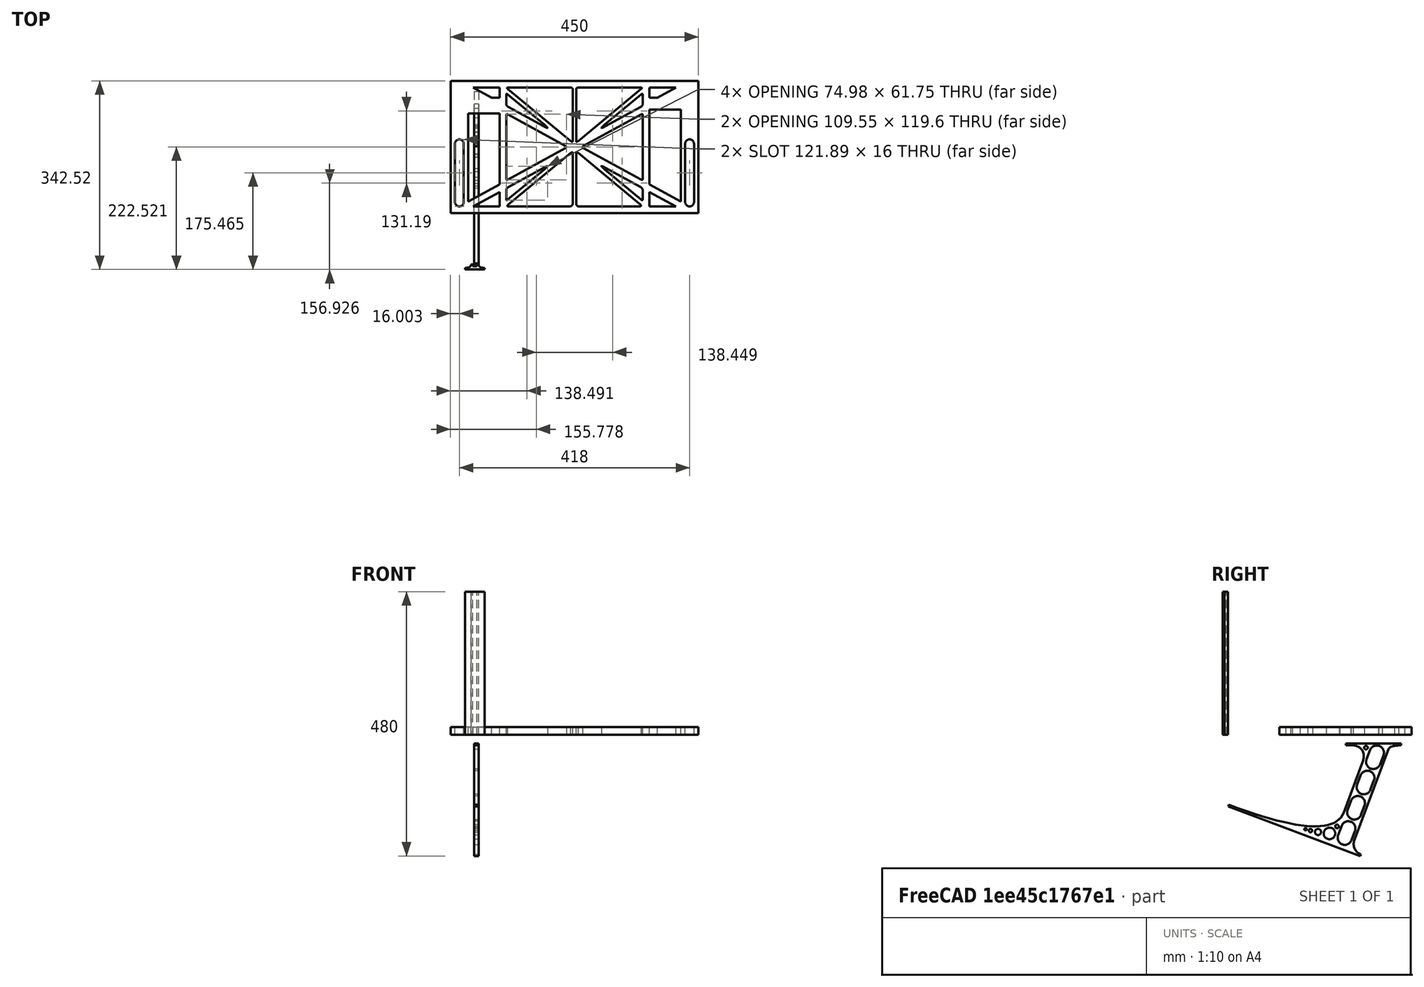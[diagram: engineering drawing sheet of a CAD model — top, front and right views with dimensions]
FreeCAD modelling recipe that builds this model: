
FCSTD DOCUMENT  (FreeCAD 0.19R0.19.2)
Label: laptopStand097
License: All rights reserved
LicenseURL: http://en.wikipedia.org/wiki/All_rights_reserved
objects: Sketcher::SketchObject×3, Part::Extrusion×3
note: 6 computed .brp shape members not serialized (recipe doc carries the construction recipe); baked Part::Feature solids carry a one-line shape summary decoded from their .brp

FEATURE [Sketcher::SketchObject] Sketch
  FullyConstrained = false
  sketch-geometry (252):
    g0: LineSegment StartX=-10.9272 StartY=-82.7794 StartZ=0 EndX=46.0728 EndY=-51.4823 EndZ=0
    g1: LineSegment StartX=366.073 StartY=-91.7794 StartZ=0 EndX=318.073 EndY=-65.424 EndZ=0
    g2: LineSegment StartX=-10.9272 StartY=77.3346 StartZ=0 EndX=-10.9272 EndY=-82.7794 EndZ=0
    g3: LineSegment StartX=375.073 StartY=-82.7794 StartZ=0 EndX=375.073 EndY=83.9235 EndZ=0
    g4: LineSegment StartX=-1.92719 StartY=-91.7794 StartZ=0 EndX=46.0728 EndY=-91.7794 EndZ=0
    g5: LineSegment StartX=318.073 StartY=124.221 StartZ=0 EndX=366.073 EndY=124.221 EndZ=0
    g6: LineSegment StartX=318.073 StartY=83.9235 StartZ=0 EndX=318.073 EndY=-51.4823 EndZ=0
    g7: LineSegment StartX=318.073 StartY=-51.4823 StartZ=0 EndX=375.073 EndY=-82.7794 EndZ=0
    g8: LineSegment StartX=318.073 StartY=-65.424 StartZ=0 EndX=318.073 EndY=-91.7794 EndZ=0
    g9: LineSegment StartX=318.073 StartY=-91.7794 StartZ=0 EndX=366.073 EndY=-91.7794 EndZ=0
    g10: LineSegment StartX=46.0728 StartY=-65.424 StartZ=0 EndX=-1.92719 EndY=-91.7794 EndZ=0
    g11: LineSegment StartX=46.0728 StartY=-65.424 StartZ=0 EndX=46.0728 EndY=-91.7794 EndZ=0
    g12: LineSegment StartX=46.0728 StartY=77.3346 StartZ=0 EndX=46.0728 EndY=-51.4823 EndZ=0
    g13: LineSegment StartX=-42.9272 StartY=136.221 StartZ=0 EndX=-42.9272 EndY=-103.779 EndZ=0
    g14: LineSegment StartX=407.073 StartY=136.221 StartZ=0 EndX=407.073 EndY=-103.779 EndZ=0
    g15: ArcOfCircle CenterX=-26.9272 CenterY=22.1087 CenterZ=0 NormalX=0 NormalY=0 NormalZ=1 AngleXU=0 Radius=8 StartAngle=1e-16 EndAngle=3.14159
    g16: ArcOfCircle CenterX=-26.9272 CenterY=-83.7794 CenterZ=0 NormalX=0 NormalY=0 NormalZ=1 AngleXU=0 Radius=8 StartAngle=3.14159 EndAngle=6.28319
    g17: LineSegment StartX=-34.9272 StartY=22.1087 StartZ=0 EndX=-34.9272 EndY=-83.7794 EndZ=0
    g18: LineSegment StartX=-18.9272 StartY=22.1087 StartZ=0 EndX=-18.9272 EndY=-83.7794 EndZ=0
    g19: ArcOfCircle CenterX=391.073 CenterY=22.1087 CenterZ=0 NormalX=0 NormalY=0 NormalZ=1 AngleXU=0 Radius=8 StartAngle=-4.4e-15 EndAngle=3.14159
    g20: LineSegment StartX=399.073 StartY=22.1087 StartZ=0 EndX=399.073 EndY=-83.7794 EndZ=0
    g21: LineSegment StartX=383.073 StartY=22.1087 StartZ=0 EndX=383.073 EndY=-83.7794 EndZ=0
    g22: ArcOfCircle CenterX=391.073 CenterY=-83.7794 CenterZ=0 NormalX=0 NormalY=0 NormalZ=1 AngleXU=0 Radius=8 StartAngle=3.14159 EndAngle=6.28319
    g23: Circle CenterX=175.022 CenterY=27.0628 CenterZ=0 NormalX=0 NormalY=0 NormalZ=1 AngleXU=0 Radius=1
    g24: Circle CenterX=179.022 CenterY=24.8665 CenterZ=0 NormalX=0 NormalY=0 NormalZ=1 AngleXU=0 Radius=1
    g25: Circle CenterX=179.022 CenterY=27.0628 CenterZ=0 NormalX=0 NormalY=0 NormalZ=1 AngleXU=0 Radius=1
    g26: BSplineCurve PolesCount=3 KnotsCount=2 Degree=2 IsPeriodic=0
    g27: GeomPoint X=175.022 Y=27.0628 Z=0
    g28: GeomPoint X=179.022 Y=27.0628 Z=0
    g29: Circle CenterX=189.124 CenterY=27.0628 CenterZ=0 NormalX=0 NormalY=0 NormalZ=1 AngleXU=0 Radius=1
    g30: Circle CenterX=185.124 CenterY=24.8665 CenterZ=0 NormalX=0 NormalY=0 NormalZ=1 AngleXU=0 Radius=1
    g31: Circle CenterX=185.124 CenterY=27.0628 CenterZ=0 NormalX=0 NormalY=0 NormalZ=1 AngleXU=0 Radius=1
    g32: BSplineCurve PolesCount=3 KnotsCount=2 Degree=2 IsPeriodic=0
    g33: GeomPoint X=189.124 Y=27.0628 Z=0
    g34: GeomPoint X=185.124 Y=27.0628 Z=0
    g35: Circle CenterX=175.022 CenterY=5.37834 CenterZ=0 NormalX=0 NormalY=0 NormalZ=1 AngleXU=0 Radius=1
    g36: Circle CenterX=179.022 CenterY=7.57463 CenterZ=0 NormalX=0 NormalY=0 NormalZ=1 AngleXU=0 Radius=1
    g37: Circle CenterX=179.022 CenterY=5.34704 CenterZ=0 NormalX=0 NormalY=0 NormalZ=1 AngleXU=0 Radius=1
    g38: BSplineCurve PolesCount=3 KnotsCount=2 Degree=2 IsPeriodic=0
    g39: GeomPoint X=175.022 Y=5.37834 Z=0
    g40: GeomPoint X=179.022 Y=5.34704 Z=0
    g41: Circle CenterX=189.124 CenterY=5.37834 CenterZ=0 NormalX=0 NormalY=0 NormalZ=1 AngleXU=0 Radius=1
    g42: Circle CenterX=185.124 CenterY=7.57463 CenterZ=0 NormalX=0 NormalY=0 NormalZ=1 AngleXU=0 Radius=1
    g43: Circle CenterX=185.124 CenterY=5.34704 CenterZ=0 NormalX=0 NormalY=0 NormalZ=1 AngleXU=0 Radius=1
    g44: BSplineCurve PolesCount=3 KnotsCount=2 Degree=2 IsPeriodic=0
    g45: GeomPoint X=189.124 Y=5.37834 Z=0
    g46: GeomPoint X=185.124 Y=5.34704 Z=0
    g47: Circle CenterX=165.871 CenterY=18.1458 CenterZ=0 NormalX=0 NormalY=0 NormalZ=1 AngleXU=0 Radius=1
    g48: Circle CenterX=169.377 CenterY=16.2206 CenterZ=0 NormalX=0 NormalY=0 NormalZ=1 AngleXU=0 Radius=1
    g49: Circle CenterX=165.871 CenterY=14.2954 CenterZ=0 NormalX=0 NormalY=0 NormalZ=1 AngleXU=0 Radius=1
    g50: BSplineCurve PolesCount=3 KnotsCount=2 Degree=2 IsPeriodic=0
    g51: GeomPoint X=165.871 Y=18.1458 Z=0
    g52: GeomPoint X=165.871 Y=14.2954 Z=0
    g53: Circle CenterX=198.275 CenterY=18.1458 CenterZ=0 NormalX=0 NormalY=0 NormalZ=1 AngleXU=0 Radius=1
    g54: Circle CenterX=194.768 CenterY=16.2206 CenterZ=0 NormalX=0 NormalY=0 NormalZ=1 AngleXU=0 Radius=1
    g55: Circle CenterX=198.275 CenterY=14.2954 CenterZ=0 NormalX=0 NormalY=0 NormalZ=1 AngleXU=0 Radius=1
    g56: BSplineCurve PolesCount=3 KnotsCount=2 Degree=2 IsPeriodic=0
    g57: GeomPoint X=198.275 Y=18.1458 Z=0
    g58: GeomPoint X=198.275 Y=14.2954 Z=0
    g59: LineSegment StartX=407.073 StartY=-103.779 StartZ=0 EndX=-42.9272 EndY=-103.779 EndZ=0
    g60: LineSegment StartX=407.073 StartY=136.221 StartZ=0 EndX=-42.9272 EndY=136.221 EndZ=0
    g61: LineSegment StartX=46.0728 StartY=77.3346 StartZ=0 EndX=-10.9272 EndY=77.3346 EndZ=0
    g62: LineSegment StartX=46.0728 StartY=105.865 StartZ=0 EndX=31.5028 EndY=105.865 EndZ=0
    g63: LineSegment StartX=46.0728 StartY=124.221 StartZ=0 EndX=46.0728 EndY=105.865 EndZ=0
    g64: LineSegment StartX=-1.92719 StartY=124.221 StartZ=0 EndX=31.5028 EndY=105.865 EndZ=0
    g65: LineSegment StartX=46.0728 StartY=124.221 StartZ=0 EndX=-1.92719 EndY=124.221 EndZ=0
    g66: LineSegment StartX=318.073 StartY=83.9235 StartZ=0 EndX=375.073 EndY=83.9235 EndZ=0
    g67: Circle CenterX=125.607 CenterY=54.1951 CenterZ=0 NormalX=0 NormalY=0 NormalZ=1 AngleXU=0 Radius=1
    g68: Circle CenterX=139.632 CenterY=46.4944 CenterZ=0 NormalX=0 NormalY=0 NormalZ=1 AngleXU=0 Radius=1
    g69: Circle CenterX=127.326 CenterY=56.7187 CenterZ=0 NormalX=0 NormalY=0 NormalZ=1 AngleXU=0 Radius=1
    g70: BSplineCurve PolesCount=3 KnotsCount=2 Degree=2 IsPeriodic=0
    g71: GeomPoint X=125.607 Y=54.1951 Z=0
    g72: GeomPoint X=127.326 Y=56.7187 Z=0
    g73: Circle CenterX=236.821 CenterY=56.7187 CenterZ=0 NormalX=0 NormalY=0 NormalZ=1 AngleXU=0 Radius=1
    g74: Circle CenterX=224.513 CenterY=46.4944 CenterZ=0 NormalX=0 NormalY=0 NormalZ=1 AngleXU=0 Radius=1
    g75: Circle CenterX=238.538 CenterY=54.1951 CenterZ=0 NormalX=0 NormalY=0 NormalZ=1 AngleXU=0 Radius=1
    g76: BSplineCurve PolesCount=3 KnotsCount=2 Degree=2 IsPeriodic=0
    g77: GeomPoint X=236.821 Y=56.7187 Z=0
    g78: GeomPoint X=238.538 Y=54.1951 Z=0
    g79: Circle CenterX=238.538 CenterY=-21.7539 CenterZ=0 NormalX=0 NormalY=0 NormalZ=1 AngleXU=0 Radius=1
    g80: Circle CenterX=224.513 CenterY=-14.0532 CenterZ=0 NormalX=0 NormalY=0 NormalZ=1 AngleXU=0 Radius=1
    g81: Circle CenterX=236.821 CenterY=-24.2775 CenterZ=0 NormalX=0 NormalY=0 NormalZ=1 AngleXU=0 Radius=1
    g82: BSplineCurve PolesCount=3 KnotsCount=2 Degree=2 IsPeriodic=0
    g83: GeomPoint X=238.538 Y=-21.7539 Z=0
    g84: GeomPoint X=236.821 Y=-24.2775 Z=0
    g85: Circle CenterX=125.607 CenterY=-21.7539 CenterZ=0 NormalX=0 NormalY=0 NormalZ=1 AngleXU=0 Radius=1
    g86: Circle CenterX=139.632 CenterY=-14.0532 CenterZ=0 NormalX=0 NormalY=0 NormalZ=1 AngleXU=0 Radius=1
    g87: Circle CenterX=127.325 CenterY=-24.2775 CenterZ=0 NormalX=0 NormalY=0 NormalZ=1 AngleXU=0 Radius=1
    g88: BSplineCurve PolesCount=3 KnotsCount=2 Degree=2 IsPeriodic=0
    g89: GeomPoint X=125.607 Y=-21.7539 Z=0
    g90: GeomPoint X=127.325 Y=-24.2775 Z=0
    g91: Circle CenterX=302.996 CenterY=111.695 CenterZ=0 NormalX=0 NormalY=0 NormalZ=1 AngleXU=0 Radius=1
    g92: Circle CenterX=306.073 CenterY=114.251 CenterZ=0 NormalX=0 NormalY=0 NormalZ=1 AngleXU=0 Radius=1
    g93: Circle CenterX=306.073 CenterY=110.251 CenterZ=0 NormalX=0 NormalY=0 NormalZ=1 AngleXU=0 Radius=1
    g94: BSplineCurve PolesCount=3 KnotsCount=2 Degree=2 IsPeriodic=0
    g95: GeomPoint X=302.996 Y=111.695 Z=0
    g96: GeomPoint X=306.073 Y=110.251 Z=0
    g97: Circle CenterX=306.073 CenterY=95.2763 CenterZ=0 NormalX=0 NormalY=0 NormalZ=1 AngleXU=0 Radius=1
    g98: Circle CenterX=306.073 CenterY=91.2763 CenterZ=0 NormalX=0 NormalY=0 NormalZ=1 AngleXU=0 Radius=1
    g99: Circle CenterX=302.567 CenterY=89.3511 CenterZ=0 NormalX=0 NormalY=0 NormalZ=1 AngleXU=0 Radius=1
    g100: BSplineCurve PolesCount=3 KnotsCount=2 Degree=2 IsPeriodic=0
    g101: GeomPoint X=306.073 Y=95.2763 Z=0
    g102: GeomPoint X=302.567 Y=89.3511 Z=0
    g103: LineSegment StartX=306.073 StartY=110.251 StartZ=0 EndX=306.073 EndY=95.2763 EndZ=0
    g104: LineSegment StartX=302.996 StartY=111.695 StartZ=0 EndX=236.821 EndY=56.7187 EndZ=0
    g105: LineSegment StartX=238.538 StartY=54.1951 StartZ=0 EndX=302.567 EndY=89.3511 EndZ=0
    g106: Circle CenterX=61.1496 CenterY=111.695 CenterZ=0 NormalX=0 NormalY=0 NormalZ=1 AngleXU=0 Radius=1
    g107: Circle CenterX=58.0728 CenterY=114.251 CenterZ=0 NormalX=0 NormalY=0 NormalZ=1 AngleXU=0 Radius=1
    g108: Circle CenterX=58.0728 CenterY=110.251 CenterZ=0 NormalX=0 NormalY=0 NormalZ=1 AngleXU=0 Radius=1
    g109: BSplineCurve PolesCount=3 KnotsCount=2 Degree=2 IsPeriodic=0
    g110: GeomPoint X=61.1496 Y=111.695 Z=0
    g111: GeomPoint X=58.0728 Y=110.251 Z=0
    g112: Circle CenterX=61.5791 CenterY=89.3511 CenterZ=0 NormalX=0 NormalY=0 NormalZ=1 AngleXU=0 Radius=1
    g113: Circle CenterX=58.0728 CenterY=91.2763 CenterZ=0 NormalX=0 NormalY=0 NormalZ=1 AngleXU=0 Radius=1
    g114: Circle CenterX=58.0728 CenterY=95.2763 CenterZ=0 NormalX=0 NormalY=0 NormalZ=1 AngleXU=0 Radius=1
    g115: BSplineCurve PolesCount=3 KnotsCount=2 Degree=2 IsPeriodic=0
    g116: GeomPoint X=61.5791 Y=89.3511 Z=0
    g117: GeomPoint X=58.0728 Y=95.2763 Z=0
    g118: LineSegment StartX=58.0728 StartY=110.251 StartZ=0 EndX=58.0728 EndY=95.2763 EndZ=0
    g119: LineSegment StartX=61.1496 StartY=111.695 StartZ=0 EndX=127.326 EndY=56.7187 EndZ=0
    g120: LineSegment StartX=125.607 StartY=54.1951 StartZ=0 EndX=61.5791 EndY=89.3511 EndZ=0
    g121: Circle CenterX=61.5791 CenterY=-56.9099 CenterZ=0 NormalX=0 NormalY=0 NormalZ=1 AngleXU=0 Radius=1
    g122: Circle CenterX=58.0728 CenterY=-58.8351 CenterZ=0 NormalX=0 NormalY=0 NormalZ=1 AngleXU=0 Radius=1
    g123: Circle CenterX=58.0728 CenterY=-62.8351 CenterZ=0 NormalX=0 NormalY=0 NormalZ=1 AngleXU=0 Radius=1
    g124: BSplineCurve PolesCount=3 KnotsCount=2 Degree=2 IsPeriodic=0
    g125: GeomPoint X=61.5791 Y=-56.9099 Z=0
    g126: GeomPoint X=58.0728 Y=-62.8351 Z=0
    g127: Circle CenterX=58.0728 CenterY=-77.8102 CenterZ=0 NormalX=0 NormalY=0 NormalZ=1 AngleXU=0 Radius=1
    g128: Circle CenterX=58.0728 CenterY=-81.8102 CenterZ=0 NormalX=0 NormalY=0 NormalZ=1 AngleXU=0 Radius=1
    g129: Circle CenterX=61.1496 CenterY=-79.2541 CenterZ=0 NormalX=0 NormalY=0 NormalZ=1 AngleXU=0 Radius=1
    g130: BSplineCurve PolesCount=3 KnotsCount=2 Degree=2 IsPeriodic=0
    g131: GeomPoint X=58.0728 Y=-77.8102 Z=0
    g132: GeomPoint X=61.1496 Y=-79.2541 Z=0
    g133: LineSegment StartX=58.0728 StartY=-62.8351 StartZ=0 EndX=58.0728 EndY=-77.8102 EndZ=0
    g134: LineSegment StartX=61.1496 StartY=-79.2541 StartZ=0 EndX=127.325 EndY=-24.2775 EndZ=0
    g135: LineSegment StartX=125.607 StartY=-21.7539 StartZ=0 EndX=61.5791 EndY=-56.9099 EndZ=0
    g136: Circle CenterX=302.567 CenterY=-56.9099 CenterZ=0 NormalX=0 NormalY=0 NormalZ=1 AngleXU=0 Radius=1
    g137: Circle CenterX=306.073 CenterY=-58.8351 CenterZ=0 NormalX=0 NormalY=0 NormalZ=1 AngleXU=0 Radius=1
    g138: Circle CenterX=306.073 CenterY=-62.8351 CenterZ=0 NormalX=0 NormalY=0 NormalZ=1 AngleXU=0 Radius=1
    g139: BSplineCurve PolesCount=3 KnotsCount=2 Degree=2 IsPeriodic=0
    g140: GeomPoint X=302.567 Y=-56.9099 Z=0
    g141: GeomPoint X=306.073 Y=-62.8351 Z=0
    g142: Circle CenterX=302.996 CenterY=-79.2541 CenterZ=0 NormalX=0 NormalY=0 NormalZ=1 AngleXU=0 Radius=1
    g143: Circle CenterX=306.073 CenterY=-81.8102 CenterZ=0 NormalX=0 NormalY=0 NormalZ=1 AngleXU=0 Radius=1
    g144: Circle CenterX=306.073 CenterY=-77.8102 CenterZ=0 NormalX=0 NormalY=0 NormalZ=1 AngleXU=0 Radius=1
    g145: BSplineCurve PolesCount=3 KnotsCount=2 Degree=2 IsPeriodic=0
    g146: GeomPoint X=302.996 Y=-79.2541 Z=0
    g147: GeomPoint X=306.073 Y=-77.8102 Z=0
    g148: LineSegment StartX=306.073 StartY=-62.8351 StartZ=0 EndX=306.073 EndY=-77.8102 EndZ=0
    g149: LineSegment StartX=302.996 StartY=-79.2541 StartZ=0 EndX=236.821 EndY=-24.2775 EndZ=0
    g150: LineSegment StartX=238.538 StartY=-21.7539 StartZ=0 EndX=302.567 EndY=-56.9099 EndZ=0
    g151: Circle CenterX=61.6457 CenterY=-88.8112 CenterZ=0 NormalX=0 NormalY=0 NormalZ=1 AngleXU=0 Radius=1
    g152: Circle CenterX=58.0728 CenterY=-91.7794 CenterZ=0 NormalX=0 NormalY=0 NormalZ=1 AngleXU=0 Radius=1
    g153: Circle CenterX=63.9135 CenterY=-91.7794 CenterZ=0 NormalX=0 NormalY=0 NormalZ=1 AngleXU=0 Radius=1
    g154: BSplineCurve PolesCount=3 KnotsCount=2 Degree=2 IsPeriodic=0
    g155: GeomPoint X=61.6457 Y=-88.8112 Z=0
    g156: GeomPoint X=63.9135 Y=-91.7794 Z=0
    g157: Circle CenterX=179.022 CenterY=-85.8163 CenterZ=0 NormalX=0 NormalY=0 NormalZ=1 AngleXU=0 Radius=1
    g158: Circle CenterX=179.022 CenterY=-91.7794 CenterZ=0 NormalX=0 NormalY=0 NormalZ=1 AngleXU=0 Radius=1
    g159: Circle CenterX=171.895 CenterY=-91.7794 CenterZ=0 NormalX=0 NormalY=0 NormalZ=1 AngleXU=0 Radius=1
    g160: BSplineCurve PolesCount=3 KnotsCount=2 Degree=2 IsPeriodic=0
    g161: GeomPoint X=179.022 Y=-85.8163 Z=0
    g162: GeomPoint X=171.895 Y=-91.7794 Z=0
    g163: Circle CenterX=185.124 CenterY=-86.2028 CenterZ=0 NormalX=0 NormalY=0 NormalZ=1 AngleXU=0 Radius=1
    g164: Circle CenterX=185.124 CenterY=-91.7794 CenterZ=0 NormalX=0 NormalY=0 NormalZ=1 AngleXU=0 Radius=1
    g165: Circle CenterX=191.747 CenterY=-91.7794 CenterZ=0 NormalX=0 NormalY=0 NormalZ=1 AngleXU=0 Radius=1
    g166: BSplineCurve PolesCount=3 KnotsCount=2 Degree=2 IsPeriodic=0
    g167: GeomPoint X=185.124 Y=-86.2028 Z=0
    g168: GeomPoint X=191.747 Y=-91.7794 Z=0
    g169: Circle CenterX=299.888 CenterY=-86.6413 CenterZ=0 NormalX=0 NormalY=0 NormalZ=1 AngleXU=0 Radius=1
    g170: Circle CenterX=306.073 CenterY=-91.7794 CenterZ=0 NormalX=0 NormalY=0 NormalZ=1 AngleXU=0 Radius=1
    g171: Circle CenterX=298.776 CenterY=-91.7794 CenterZ=0 NormalX=0 NormalY=0 NormalZ=1 AngleXU=0 Radius=1
    g172: BSplineCurve PolesCount=3 KnotsCount=2 Degree=2 IsPeriodic=0
    g173: GeomPoint X=299.888 Y=-86.6413 Z=0
    g174: GeomPoint X=298.776 Y=-91.7794 Z=0
    g175: LineSegment StartX=189.124 StartY=5.37834 StartZ=0 EndX=299.888 EndY=-86.6413 EndZ=0
    g176: LineSegment StartX=298.776 StartY=-91.7794 StartZ=0 EndX=191.747 EndY=-91.7794 EndZ=0
    g177: LineSegment StartX=185.124 StartY=-86.2028 StartZ=0 EndX=185.124 EndY=5.34704 EndZ=0
    g178: LineSegment StartX=179.022 StartY=5.34704 StartZ=0 EndX=179.022 EndY=-85.8163 EndZ=0
    g179: LineSegment StartX=171.895 StartY=-91.7794 StartZ=0 EndX=63.9135 EndY=-91.7794 EndZ=0
    g180: LineSegment StartX=61.6457 StartY=-88.8112 StartZ=0 EndX=175.022 EndY=5.37834 EndZ=0
    g181: Circle CenterX=302.073 CenterY=124.221 CenterZ=0 NormalX=0 NormalY=0 NormalZ=1 AngleXU=0 Radius=1
    g182: Circle CenterX=306.073 CenterY=124.221 CenterZ=0 NormalX=0 NormalY=0 NormalZ=1 AngleXU=0 Radius=1
    g183: Circle CenterX=302.996 CenterY=121.665 CenterZ=0 NormalX=0 NormalY=0 NormalZ=1 AngleXU=0 Radius=1
    g184: BSplineCurve PolesCount=3 KnotsCount=2 Degree=2 IsPeriodic=0
    g185: GeomPoint X=302.073 Y=124.221 Z=0
    g186: GeomPoint X=302.996 Y=121.665 Z=0
    g187: Circle CenterX=189.124 CenterY=124.221 CenterZ=0 NormalX=0 NormalY=0 NormalZ=1 AngleXU=0 Radius=1
    g188: Circle CenterX=185.124 CenterY=124.221 CenterZ=0 NormalX=0 NormalY=0 NormalZ=1 AngleXU=0 Radius=1
    g189: Circle CenterX=185.124 CenterY=120.221 CenterZ=0 NormalX=0 NormalY=0 NormalZ=1 AngleXU=0 Radius=1
    g190: BSplineCurve PolesCount=3 KnotsCount=2 Degree=2 IsPeriodic=0
    g191: GeomPoint X=189.124 Y=124.221 Z=0
    g192: GeomPoint X=185.124 Y=120.221 Z=0
    g193: Circle CenterX=175.022 CenterY=124.221 CenterZ=0 NormalX=0 NormalY=0 NormalZ=1 AngleXU=0 Radius=1
    g194: Circle CenterX=179.022 CenterY=124.221 CenterZ=0 NormalX=0 NormalY=0 NormalZ=1 AngleXU=0 Radius=1
    g195: Circle CenterX=179.022 CenterY=120.221 CenterZ=0 NormalX=0 NormalY=0 NormalZ=1 AngleXU=0 Radius=1
    g196: BSplineCurve PolesCount=3 KnotsCount=2 Degree=2 IsPeriodic=0
    g197: GeomPoint X=175.022 Y=124.221 Z=0
    g198: GeomPoint X=179.022 Y=120.221 Z=0
    g199: Circle CenterX=62.0728 CenterY=124.221 CenterZ=0 NormalX=0 NormalY=0 NormalZ=1 AngleXU=0 Radius=1
    g200: Circle CenterX=58.0728 CenterY=124.221 CenterZ=0 NormalX=0 NormalY=0 NormalZ=1 AngleXU=0 Radius=1
    g201: Circle CenterX=61.1496 CenterY=121.665 CenterZ=0 NormalX=0 NormalY=0 NormalZ=1 AngleXU=0 Radius=1
    g202: BSplineCurve PolesCount=3 KnotsCount=2 Degree=2 IsPeriodic=0
    g203: GeomPoint X=62.0728 Y=124.221 Z=0
    g204: GeomPoint X=61.1496 Y=121.665 Z=0
    g205: LineSegment StartX=62.0728 StartY=124.221 StartZ=0 EndX=175.022 EndY=124.221 EndZ=0
    g206: LineSegment StartX=179.022 StartY=120.221 StartZ=0 EndX=179.022 EndY=27.0628 EndZ=0
    g207: LineSegment StartX=185.124 StartY=27.0628 StartZ=0 EndX=185.124 EndY=120.221 EndZ=0
    g208: LineSegment StartX=189.124 StartY=124.221 StartZ=0 EndX=302.073 EndY=124.221 EndZ=0
    g209: LineSegment StartX=302.996 StartY=121.665 StartZ=0 EndX=189.124 EndY=27.0628 EndZ=0
    g210: LineSegment StartX=175.022 StartY=27.0628 StartZ=0 EndX=61.1496 EndY=121.665 EndZ=0
    g211: Circle CenterX=61.5791 CenterY=75.4095 CenterZ=0 NormalX=0 NormalY=0 NormalZ=1 AngleXU=0 Radius=1
    g212: Circle CenterX=58.0728 CenterY=77.3346 CenterZ=0 NormalX=0 NormalY=0 NormalZ=1 AngleXU=0 Radius=1
    g213: Circle CenterX=58.0728 CenterY=73.3346 CenterZ=0 NormalX=0 NormalY=0 NormalZ=1 AngleXU=0 Radius=1
    g214: BSplineCurve PolesCount=3 KnotsCount=2 Degree=2 IsPeriodic=0
    g215: GeomPoint X=61.5791 Y=75.4095 Z=0
    g216: GeomPoint X=58.0728 Y=73.3346 Z=0
    g217: Circle CenterX=58.0728 CenterY=-40.8935 CenterZ=0 NormalX=0 NormalY=0 NormalZ=1 AngleXU=0 Radius=1
    g218: Circle CenterX=58.0728 CenterY=-44.8935 CenterZ=0 NormalX=0 NormalY=0 NormalZ=1 AngleXU=0 Radius=1
    g219: Circle CenterX=61.5791 CenterY=-42.9683 CenterZ=0 NormalX=0 NormalY=0 NormalZ=1 AngleXU=0 Radius=1
    g220: BSplineCurve PolesCount=3 KnotsCount=2 Degree=2 IsPeriodic=0
    g221: GeomPoint X=58.0728 Y=-40.8935 Z=0
    g222: GeomPoint X=61.5791 Y=-42.9683 Z=0
    g223: LineSegment StartX=61.5791 StartY=-42.9683 StartZ=0 EndX=165.871 EndY=14.2954 EndZ=0
    g224: LineSegment StartX=165.871 StartY=18.1458 StartZ=0 EndX=61.5791 EndY=75.4095 EndZ=0
    g225: LineSegment StartX=58.0728 StartY=73.3346 StartZ=0 EndX=58.0728 EndY=-40.8935 EndZ=0
    g226: Circle CenterX=302.567 CenterY=-42.9683 CenterZ=0 NormalX=0 NormalY=0 NormalZ=1 AngleXU=0 Radius=1
    g227: Circle CenterX=306.073 CenterY=-44.8935 CenterZ=0 NormalX=0 NormalY=0 NormalZ=1 AngleXU=0 Radius=1
    g228: Circle CenterX=306.073 CenterY=-40.8935 CenterZ=0 NormalX=0 NormalY=0 NormalZ=1 AngleXU=0 Radius=1
    g229: BSplineCurve PolesCount=3 KnotsCount=2 Degree=2 IsPeriodic=0
    g230: GeomPoint X=302.567 Y=-42.9683 Z=0
    g231: GeomPoint X=306.073 Y=-40.8935 Z=0
    g232: Circle CenterX=306.073 CenterY=73.3346 CenterZ=0 NormalX=0 NormalY=0 NormalZ=1 AngleXU=0 Radius=1
    g233: Circle CenterX=306.073 CenterY=77.3346 CenterZ=0 NormalX=0 NormalY=0 NormalZ=1 AngleXU=0 Radius=1
    g234: Circle CenterX=302.567 CenterY=75.4095 CenterZ=0 NormalX=0 NormalY=0 NormalZ=1 AngleXU=0 Radius=1
    g235: BSplineCurve PolesCount=3 KnotsCount=2 Degree=2 IsPeriodic=0
    g236: GeomPoint X=306.073 Y=73.3346 Z=0
    g237: GeomPoint X=302.567 Y=75.4095 Z=0
    g238: LineSegment StartX=302.567 StartY=-42.9683 StartZ=0 EndX=198.275 EndY=14.2954 EndZ=0
    g239: LineSegment StartX=198.275 StartY=18.1458 StartZ=0 EndX=302.567 EndY=75.4095 EndZ=0
    g240: LineSegment StartX=306.073 StartY=73.3346 StartZ=0 EndX=306.073 EndY=-40.8935 EndZ=0
    g241: LineSegment StartX=318.073 StartY=124.221 StartZ=0 EndX=322.073 EndY=124.221 EndZ=0
    g242: LineSegment StartX=366.073 StartY=124.221 StartZ=0 EndX=362.073 EndY=124.221 EndZ=0
    g243: LineSegment StartX=328.643 StartY=105.865 StartZ=0 EndX=332.643 EndY=105.865 EndZ=0
    g244: LineSegment StartX=332.651 StartY=105.853 StartZ=0 EndX=336.157 EndY=107.779 EndZ=0
    g245: LineSegment StartX=366.073 StartY=124.221 StartZ=0 EndX=362.567 EndY=122.294 EndZ=0
    g246: LineSegment StartX=318.073 StartY=105.865 StartZ=0 EndX=318.073 EndY=109.865 EndZ=0
    g247: LineSegment StartX=318.073 StartY=105.865 StartZ=0 EndX=322.073 EndY=105.865 EndZ=0
    g248: LineSegment StartX=318.073 StartY=124.221 StartZ=0 EndX=318.073 EndY=120.221 EndZ=0
    g249: LineSegment StartX=332.651 StartY=105.853 StartZ=0 EndX=366.073 EndY=124.221 EndZ=0
    g250: LineSegment StartX=322.073 StartY=105.865 StartZ=0 EndX=328.643 EndY=105.865 EndZ=0
    g251: LineSegment StartX=318.073 StartY=120.221 StartZ=0 EndX=318.073 EndY=109.865 EndZ=0
  constraints (436):
    c: Horizontal(g4)
    c: Coincident(g6,g7)
    c: Coincident(g8,g1)
    c: Tangent(g6,g8)
    c: Coincident(g11,g10)
    c: Coincident(g0,g12)
    c: Block(g7)
    c: Block(g3)
    c: Block(g1)
    c: Block(g8)
    c: Block(g11)
    c: Block(g10)
    c: Block(g0)
    c: Block(g2)
    c: Block(g5)
    c: Block(g9)
    c: Block(g4)
    c: Vertical(g13)
    c: Vertical(g14)
    c: Block(g14)
    c: Block(g13)
    c: Tangent(g15,g18) = 1.5708
    c: Tangent(g15,g17) = -1.5708
    c: Tangent(g17,g16) = -1.5708
    c: Tangent(g18,g16) = 1.5708
    c: Vertical(g17)
    c: Equal(g15,g16)
    c: Block(g18)
    c: Block(g17)
    c: Tangent(g19,g20) = 1.5708
    c: Tangent(g20,g22) = 1.5708
    c: Equal(g19,g22)
    c: Coincident(g21,g19)
    c: Coincident(g21,g22)
    c: Block(g20)
    c: Block(g21)
    c: Weight(g23) = 1
    c: Equal(g23,g24)
    c: Equal(g23,g25)
    c: InternalAlignment(g23,g26)
    c: InternalAlignment(g24,g26)
    c: InternalAlignment(g25,g26)
    c: InternalAlignment(g27,g26)
    c: InternalAlignment(g28,g26)
    c: Weight(g29) = 1
    c: Equal(g29,g30)
    c: Equal(g29,g31)
    c: InternalAlignment(g29,g32)
    c: InternalAlignment(g30,g32)
    c: InternalAlignment(g31,g32)
    c: InternalAlignment(g33,g32)
    c: InternalAlignment(g34,g32)
    c: Block(g32)
    c: Block(g26)
    c: Weight(g35) = 1
    c: Equal(g35,g36)
    c: Equal(g35,g37)
    c: InternalAlignment(g35,g38)
    c: InternalAlignment(g36,g38)
    c: InternalAlignment(g37,g38)
    c: InternalAlignment(g39,g38)
    c: InternalAlignment(g40,g38)
    c: Weight(g41) = 1
    c: Equal(g41,g42)
    c: Equal(g41,g43)
    c: InternalAlignment(g41,g44)
    c: InternalAlignment(g42,g44)
    c: InternalAlignment(g43,g44)
    c: InternalAlignment(g45,g44)
    c: InternalAlignment(g46,g44)
    c: Block(g44)
    c: Block(g38)
    c: Weight(g47) = 1
    c: Equal(g47,g48)
    c: Equal(g47,g49)
    c: InternalAlignment(g47,g50)
    c: InternalAlignment(g48,g50)
    c: InternalAlignment(g49,g50)
    c: InternalAlignment(g51,g50)
    c: InternalAlignment(g52,g50)
    c: Weight(g53) = 1
    c: Equal(g53,g54)
    c: Equal(g53,g55)
    c: InternalAlignment(g53,g56)
    c: InternalAlignment(g54,g56)
    c: InternalAlignment(g55,g56)
    c: InternalAlignment(g57,g56)
    c: InternalAlignment(g58,g56)
    c: Block(g50)
    c: Block(g56)
    c: Coincident(g59,g14)
    c: Coincident(g59,g13)
    c: Horizontal(g59)
    c: Distance(g59) = 450
    c: Coincident(g60,g14)
    c: Coincident(g60,g13)
    c: Horizontal(g60)
    c: Horizontal(g61)
    c: Coincident(g12,g61)
    c: Horizontal(g62)
    c: Vertical(g63)
    c: Block(g63)
    c: Block(g62)
    c: Block(g61)
    c: Distance(g63) = 18.3554
    c: Coincident(g65,g63)
    c: Coincident(g65,g64)
    c: Horizontal(g65)
    c: Block(g65)
    c: Block(g64)
    c: Coincident(g62,g64)
    c: Coincident(g2,g61)
    c: Coincident(g66,g6)
    c: Horizontal(g66)
    c: Block(g66)
    c: Coincident(g3,g66)
    c: Weight(g67) = 1
    c: Equal(g67,g68)
    c: Equal(g67,g69)
    c: InternalAlignment(g67,g70)
    c: InternalAlignment(g68,g70)
    c: InternalAlignment(g69,g70)
    c: InternalAlignment(g71,g70)
    c: InternalAlignment(g72,g70)
    c: Block(g70)
    c: Weight(g73) = 1
    c: Equal(g73,g74)
    c: Equal(g73,g75)
    c: InternalAlignment(g73,g76)
    c: InternalAlignment(g74,g76)
    c: InternalAlignment(g75,g76)
    c: InternalAlignment(g77,g76)
    c: InternalAlignment(g78,g76)
    c: Block(g76)
    c: Weight(g79) = 1
    c: Equal(g79,g80)
    c: Equal(g79,g81)
    c: InternalAlignment(g79,g82)
    c: InternalAlignment(g80,g82)
    c: InternalAlignment(g81,g82)
    c: InternalAlignment(g83,g82)
    c: InternalAlignment(g84,g82)
    c: Block(g82)
    c: Weight(g85) = 1
    c: Equal(g85,g86)
    c: Equal(g85,g87)
    c: InternalAlignment(g85,g88)
    c: InternalAlignment(g86,g88)
    c: InternalAlignment(g87,g88)
    c: InternalAlignment(g89,g88)
    c: InternalAlignment(g90,g88)
    c: Block(g88)
    c: Weight(g91) = 1
    c: Equal(g91,g92)
    c: Equal(g91,g93)
    c: InternalAlignment(g91,g94)
    c: InternalAlignment(g92,g94)
    c: InternalAlignment(g93,g94)
    c: InternalAlignment(g95,g94)
    c: InternalAlignment(g96,g94)
    c: Weight(g97) = 1
    c: Equal(g97,g98)
    c: Equal(g97,g99)
    c: InternalAlignment(g97,g100)
    c: InternalAlignment(g98,g100)
    c: InternalAlignment(g99,g100)
    c: InternalAlignment(g101,g100)
    c: InternalAlignment(g102,g100)
    c: Block(g94)
    c: Block(g100)
    c: Coincident(g103,g94)
    c: Coincident(g103,g100)
    c: Vertical(g103)
    c: Coincident(g104,g94)
    c: Coincident(g104,g76)
    c: Coincident(g105,g76)
    c: Coincident(g105,g100)
    c: Weight(g106) = 1
    c: Equal(g106,g107)
    c: Equal(g106,g108)
    c: InternalAlignment(g106,g109)
    c: InternalAlignment(g107,g109)
    c: InternalAlignment(g108,g109)
    c: InternalAlignment(g110,g109)
    c: InternalAlignment(g111,g109)
    c: Weight(g112) = 1
    c: Equal(g112,g113)
    c: Equal(g112,g114)
    c: InternalAlignment(g112,g115)
    c: InternalAlignment(g113,g115)
    c: InternalAlignment(g114,g115)
    c: InternalAlignment(g116,g115)
    c: InternalAlignment(g117,g115)
    c: Block(g109)
    c: Block(g115)
    c: Coincident(g118,g109)
    c: Coincident(g118,g115)
    c: Vertical(g118)
    c: Coincident(g119,g109)
    c: Coincident(g119,g70)
    c: Coincident(g120,g70)
    c: Coincident(g120,g115)
    c: Weight(g121) = 1
    c: Equal(g121,g122)
    c: Equal(g121,g123)
    c: InternalAlignment(g121,g124)
    c: InternalAlignment(g122,g124)
    c: InternalAlignment(g123,g124)
    c: InternalAlignment(g125,g124)
    c: InternalAlignment(g126,g124)
    c: Weight(g127) = 1
    c: Equal(g127,g128)
    c: Equal(g127,g129)
    c: InternalAlignment(g127,g130)
    c: InternalAlignment(g128,g130)
    c: InternalAlignment(g129,g130)
    c: InternalAlignment(g131,g130)
    c: InternalAlignment(g132,g130)
    c: Block(g124)
    c: Block(g130)
    c: Coincident(g133,g124)
    c: Coincident(g133,g130)
    c: Vertical(g133)
    c: Coincident(g134,g130)
    c: Coincident(g134,g88)
    c: Coincident(g135,g88)
    c: Coincident(g135,g124)
    c: Weight(g136) = 1
    c: Equal(g136,g137)
    c: Equal(g136,g138)
    c: InternalAlignment(g136,g139)
    c: InternalAlignment(g137,g139)
    c: InternalAlignment(g138,g139)
    c: InternalAlignment(g140,g139)
    c: InternalAlignment(g141,g139)
    c: Weight(g142) = 1
    c: Equal(g142,g143)
    c: Equal(g142,g144)
    c: InternalAlignment(g142,g145)
    c: InternalAlignment(g143,g145)
    c: InternalAlignment(g144,g145)
    c: InternalAlignment(g146,g145)
    c: InternalAlignment(g147,g145)
    c: Block(g139)
    c: Block(g145)
    c: Coincident(g148,g139)
    c: Coincident(g148,g145)
    c: Vertical(g148)
    c: Coincident(g149,g145)
    c: Coincident(g149,g82)
    c: Coincident(g150,g82)
    c: Coincident(g150,g139)
    c: Weight(g151) = 1
    c: Equal(g151,g152)
    c: Equal(g151,g153)
    c: InternalAlignment(g151,g154)
    c: InternalAlignment(g152,g154)
    c: InternalAlignment(g153,g154)
    c: InternalAlignment(g155,g154)
    c: InternalAlignment(g156,g154)
    c: Weight(g157) = 1
    c: Equal(g157,g158)
    c: Equal(g157,g159)
    c: InternalAlignment(g157,g160)
    c: InternalAlignment(g158,g160)
    c: InternalAlignment(g159,g160)
    c: InternalAlignment(g161,g160)
    c: InternalAlignment(g162,g160)
    c: Weight(g163) = 1
    c: Equal(g163,g164)
    c: Equal(g163,g165)
    c: InternalAlignment(g163,g166)
    c: InternalAlignment(g164,g166)
    c: InternalAlignment(g165,g166)
    c: InternalAlignment(g167,g166)
    c: InternalAlignment(g168,g166)
    c: Weight(g169) = 1
    c: Equal(g169,g170)
    c: Equal(g169,g171)
    c: InternalAlignment(g169,g172)
    c: InternalAlignment(g170,g172)
    c: InternalAlignment(g171,g172)
    c: InternalAlignment(g173,g172)
    c: InternalAlignment(g174,g172)
    c: Block(g172)
    c: Block(g166)
    c: Block(g160)
    c: Block(g154)
    c: Coincident(g175,g44)
    c: Coincident(g175,g172)
    c: Coincident(g176,g172)
    c: Coincident(g176,g166)
    c: Horizontal(g176)
    c: Coincident(g177,g166)
    c: Coincident(g177,g44)
    c: Vertical(g177)
    c: Coincident(g178,g38)
    c: Coincident(g178,g160)
    c: Vertical(g178)
    c: Coincident(g179,g160)
    c: Coincident(g179,g154)
    c: Horizontal(g179)
    c: Coincident(g180,g154)
    c: Coincident(g180,g38)
    c: Weight(g181) = 1
    c: Equal(g181,g182)
    c: Equal(g181,g183)
    c: InternalAlignment(g181,g184)
    c: InternalAlignment(g182,g184)
    c: InternalAlignment(g183,g184)
    c: InternalAlignment(g185,g184)
    c: InternalAlignment(g186,g184)
    c: Weight(g187) = 1
    c: Equal(g187,g188)
    c: Equal(g187,g189)
    c: InternalAlignment(g187,g190)
    c: InternalAlignment(g188,g190)
    c: InternalAlignment(g189,g190)
    c: InternalAlignment(g191,g190)
    c: InternalAlignment(g192,g190)
    c: Weight(g193) = 1
    c: Equal(g193,g194)
    c: Equal(g193,g195)
    c: InternalAlignment(g193,g196)
    c: InternalAlignment(g194,g196)
    c: InternalAlignment(g195,g196)
    c: InternalAlignment(g197,g196)
    c: InternalAlignment(g198,g196)
    c: Weight(g199) = 1
    c: Equal(g199,g200)
    c: Equal(g199,g201)
    c: InternalAlignment(g199,g202)
    c: InternalAlignment(g200,g202)
    c: InternalAlignment(g201,g202)
    c: InternalAlignment(g203,g202)
    c: InternalAlignment(g204,g202)
    c: Block(g202)
    c: Block(g196)
    c: Block(g190)
    c: Block(g184)
    c: Coincident(g205,g202)
    c: Coincident(g205,g196)
    c: Horizontal(g205)
    c: Coincident(g206,g196)
    c: Coincident(g206,g26)
    c: Vertical(g206)
    c: Coincident(g207,g32)
    c: Coincident(g207,g190)
    c: Vertical(g207)
    c: Coincident(g208,g190)
    c: Coincident(g208,g184)
    c: Horizontal(g208)
    c: Coincident(g209,g184)
    c: Coincident(g209,g32)
    c: Coincident(g210,g26)
    c: Weight(g211) = 1
    c: Equal(g211,g212)
    c: Equal(g211,g213)
    c: InternalAlignment(g211,g214)
    c: InternalAlignment(g212,g214)
    c: InternalAlignment(g213,g214)
    c: InternalAlignment(g215,g214)
    c: InternalAlignment(g216,g214)
    c: Weight(g217) = 1
    c: Equal(g217,g218)
    c: Equal(g217,g219)
    c: InternalAlignment(g217,g220)
    c: InternalAlignment(g218,g220)
    c: InternalAlignment(g219,g220)
    c: InternalAlignment(g221,g220)
    c: InternalAlignment(g222,g220)
    c: Block(g220)
    c: Block(g214)
    c: Coincident(g223,g220)
    c: Coincident(g223,g50)
    c: Coincident(g224,g50)
    c: Coincident(g224,g214)
    c: Coincident(g225,g214)
    c: Coincident(g225,g220)
    c: Vertical(g225)
    c: Weight(g226) = 1
    c: Equal(g226,g227)
    c: Equal(g226,g228)
    c: InternalAlignment(g226,g229)
    c: InternalAlignment(g227,g229)
    c: InternalAlignment(g228,g229)
    c: InternalAlignment(g230,g229)
    c: InternalAlignment(g231,g229)
    c: Weight(g232) = 1
    c: Equal(g232,g233)
    c: Equal(g232,g234)
    c: InternalAlignment(g232,g235)
    c: InternalAlignment(g233,g235)
    c: InternalAlignment(g234,g235)
    c: InternalAlignment(g236,g235)
    c: InternalAlignment(g237,g235)
    c: Block(g235)
    c: Block(g229)
    c: Coincident(g238,g229)
    c: Coincident(g238,g56)
    c: Coincident(g239,g56)
    c: Coincident(g239,g235)
    c: Coincident(g240,g235)
    c: Coincident(g240,g229)
    c: Vertical(g240)
    c: Horizontal(g241)
    c: Horizontal(g242)
    c: Horizontal(g243)
    c: Vertical(g246)
    c: Horizontal(g247)
    c: Vertical(g248)
    c: Distance(g243) = 4
    c: Distance(g247) = 4
    c: Distance(g246) = 4
    c: Distance(g248) = 4
    c: Distance(g241) = 4
    c: Distance(g242) = 4
    c: Coincident(g241,g5)
    c: Coincident(g248,g5)
    c: Coincident(g5,g242)
    c: Coincident(g249,g5)
    c: Coincident(g250,g247)
    c: Coincident(g250,g243)
    c: Horizontal(g250)
    c: Block(g250)
    c: Coincident(g251,g248)
    c: Coincident(g251,g246)
    c: Vertical(g251)
    c: Block(g251)
    c: Distance(g244) = 4
    c: Distance(g245) = 4
    c: Parallel(g244,g249)
    c: Parallel(g245,g249)
    c: Block(g249)
    c: Coincident(g244,g249)
    c: Coincident(g245,g5)
FEATURE [Sketcher::SketchObject] Sketch001
  FullyConstrained = true
  MapMode = 4
  Placement = pos=(0,0,0) rot=(0.57735,0.57735,0.57735;2.0944rad)
  Support = -> [Sketch]
  sketch-geometry (46):
    g0: BSplineCurve PolesCount=3 KnotsCount=2 Degree=2 IsPeriodic=0
    g1: ArcOfCircle CenterX=73.1223 CenterY=-32.291 CenterZ=0 NormalX=0 NormalY=0 NormalZ=1 AngleXU=0 Radius=13 StartAngle=5.92268 EndAngle=9.06428
    g2: ArcOfCircle CenterX=66.7816 CenterY=-49.1439 CenterZ=0 NormalX=0 NormalY=0 NormalZ=1 AngleXU=0 Radius=13 StartAngle=2.78068 EndAngle=5.92131
    g3: ArcOfCircle CenterX=55.9263 CenterY=-78.1807 CenterZ=0 NormalX=0 NormalY=0 NormalZ=1 AngleXU=0 Radius=13 StartAngle=5.92268 EndAngle=9.06428
    g4: ArcOfCircle CenterX=49.5884 CenterY=-95.0342 CenterZ=0 NormalX=0 NormalY=0 NormalZ=1 AngleXU=0 Radius=13 StartAngle=2.78068 EndAngle=5.92131
    g5: ArcOfCircle CenterX=38.7206 CenterY=-124.067 CenterZ=0 NormalX=0 NormalY=0 NormalZ=1 AngleXU=0 Radius=13 StartAngle=5.92268 EndAngle=9.06428
    g6: ArcOfCircle CenterX=32.3875 CenterY=-140.92 CenterZ=0 NormalX=0 NormalY=0 NormalZ=1 AngleXU=0 Radius=13 StartAngle=2.78068 EndAngle=5.92131
    g7: ArcOfCircle CenterX=21.4715 CenterY=-169.934 CenterZ=0 NormalX=0 NormalY=0 NormalZ=1 AngleXU=0 Radius=13 StartAngle=5.92268 EndAngle=9.06428
    g8: ArcOfCircle CenterX=15.1336 CenterY=-186.787 CenterZ=0 NormalX=0 NormalY=0 NormalZ=1 AngleXU=0 Radius=13 StartAngle=2.78068 EndAngle=5.92131
    g9-g12: Circle x4 (B-spline internal-alignment scaffolding for g13; pole/knot coordinates omitted)
    g13: BSplineCurve PolesCount=4 KnotsCount=2 Degree=3 IsPeriodic=0
    g14: GeomPoint X=28.8094 Y=-19.0875 Z=0
    g15: GeomPoint X=47.0443 Y=-50.4712 Z=0
    g16: Circle CenterX=53.5586 CenterY=-23.2695 CenterZ=0 NormalX=0 NormalY=0 NormalZ=1 AngleXU=0 Radius=3.24518
    g17: Circle CenterX=-195.441 CenterY=-127.082 CenterZ=0 NormalX=0 NormalY=0 NormalZ=1 AngleXU=0 Radius=1
    g18: Circle CenterX=-8.24091 CenterY=-197.481 CenterZ=0 NormalX=0 NormalY=0 NormalZ=1 AngleXU=0 Radius=1
    g19: Circle CenterX=12.8789 CenterY=-141.321 CenterZ=0 NormalX=0 NormalY=0 NormalZ=1 AngleXU=0 Radius=1
    g20: BSplineCurve PolesCount=3 KnotsCount=2 Degree=2 IsPeriodic=0
    g21: GeomPoint X=-195.441 Y=-127.082 Z=0
    g22: GeomPoint X=12.8789 Y=-141.321 Z=0
    g23: Circle CenterX=-12.8016 CenterY=-179.036 CenterZ=0 NormalX=0 NormalY=0 NormalZ=1 AngleXU=0 Radius=10.5072
    g24: Circle CenterX=0.933922 CenterY=-166.43 CenterZ=0 NormalX=0 NormalY=0 NormalZ=1 AngleXU=0 Radius=3.26661
    g25: Circle CenterX=-33.5518 CenterY=-176.44 CenterZ=0 NormalX=0 NormalY=0 NormalZ=1 AngleXU=0 Radius=5.64388
    g26: Circle CenterX=-47.2366 CenterY=-173.859 CenterZ=0 NormalX=0 NormalY=0 NormalZ=1 AngleXU=0 Radius=3.01653
    g27: Circle CenterX=-56.2595 CenterY=-171.456 CenterZ=0 NormalX=0 NormalY=0 NormalZ=1 AngleXU=0 Radius=2.12826
    g28: ArcOfCircle CenterX=51.2151 CenterY=-198.473 CenterZ=0 NormalX=0 NormalY=0 NormalZ=1 AngleXU=0 Radius=20 StartAngle=2.78189 EndAngle=4.35269
    g29: LineSegment StartX=32.4951 StartY=-191.433 StartZ=0 EndX=94.6578 EndY=-26.1352 EndZ=0
    g30: LineSegment StartX=43.1192 StartY=-220.001 StartZ=0 EndX=-196.497 EndY=-129.89 EndZ=0
    g31: LineSegment StartX=43.1192 StartY=-220.001 StartZ=0 EndX=44.1752 EndY=-217.193 EndZ=0
    g32: LineSegment StartX=117.223 StartY=-19.0875 StartZ=0 EndX=117.223 EndY=-16.0875 EndZ=0
    g33: LineSegment StartX=117.223 StartY=-16.0875 StartZ=0 EndX=17.2232 EndY=-16.0875 EndZ=0
    g34: LineSegment StartX=17.2232 StartY=-16.0875 StartZ=0 EndX=17.2232 EndY=-19.0875 EndZ=0
    g35: LineSegment StartX=28.8094 StartY=-19.0875 StartZ=0 EndX=17.2232 EndY=-19.0875 EndZ=0
    g36: LineSegment StartX=47.0443 StartY=-50.4712 StartZ=0 EndX=12.8789 EndY=-141.321 EndZ=0
    g37: LineSegment StartX=-195.441 StartY=-127.082 StartZ=0 EndX=-196.497 EndY=-129.89 EndZ=0
    g38: LineSegment StartX=85.2866 StartY=-36.8766 StartZ=0 EndX=78.9396 EndY=-53.7463 EndZ=0
    g39: LineSegment StartX=60.9579 StartY=-27.7053 StartZ=0 EndX=54.6191 EndY=-44.5532 EndZ=0
    g40: LineSegment StartX=68.0907 StartY=-82.7664 StartZ=0 EndX=61.7465 EndY=-99.6365 EndZ=0
    g41: LineSegment StartX=43.7619 StartY=-73.595 StartZ=0 EndX=37.426 EndY=-90.4435 EndZ=0
    g42: LineSegment StartX=50.885 StartY=-128.652 StartZ=0 EndX=44.5456 EndY=-145.522 EndZ=0
    g43: LineSegment StartX=26.5562 StartY=-119.481 StartZ=0 EndX=20.2251 EndY=-136.329 EndZ=0
    g44: LineSegment StartX=9.3071 StartY=-165.349 StartZ=0 EndX=2.97115 EndY=-182.197 EndZ=0
    g45: LineSegment StartX=33.6358 StartY=-174.52 StartZ=0 EndX=27.2917 EndY=-191.39 EndZ=0
  constraints (71):
    c: Block(g0)
    c: Block(g1)
    c: Block(g2)
    c: Block(g4)
    c: Block(g3)
    c: Block(g6)
    c: Block(g5)
    c: Block(g8)
    c: Block(g7)
    c: Weight(g9) = 1
    c: Equal(g9,g10)
    c: Equal(g9,g11)
    c: Equal(g9,g12)
    c: InternalAlignment(g9-g12 -> g13) x4
    c: InternalAlignment(g14,g13)
    c: InternalAlignment(g15,g13)
    c: Block(g16)
    c: Weight(g17) = 1
    c: Equal(g17,g18)
    c: Equal(g17,g19)
    c: InternalAlignment(g17,g20)
    c: InternalAlignment(g18,g20)
    c: InternalAlignment(g19,g20)
    c: InternalAlignment(g21,g20)
    c: InternalAlignment(g22,g20)
    c: Block(g20)
    c: Block(g23)
    c: Block(g24)
    c: Block(g25)
    c: Block(g26)
    c: Block(g27)
    c: Block(g28)
    c: Coincident(g29,g28)
    c: Coincident(g29,g0)
    c: Block(g13)
    c: Coincident(g31,g30)
    c: Coincident(g31,g28)
    c: Block(g31)
    c: Coincident(g32,g0)
    c: Vertical(g32)
    c: Coincident(g33,g32)
    c: Horizontal(g33)
    c: Coincident(g34,g33)
    c: Vertical(g34)
    c: Block(g33)
    c: Coincident(g35,g13)
    c: Coincident(g35,g34)
    c: Horizontal(g35)
    c: Coincident(g36,g13)
    c: Coincident(g36,g20)
    c: Coincident(g37,g20)
    c: Coincident(g37,g30)
    c: Block(g30)
    c: Coincident(g38,g1)
    c: Coincident(g38,g2)
    c: Coincident(g39,g1)
    c: Coincident(g39,g2)
    c: Coincident(g40,g3)
    c: Coincident(g40,g4)
    c: Coincident(g41,g3)
    c: Coincident(g41,g4)
    c: Coincident(g42,g5)
    c: Coincident(g42,g6)
    c: Coincident(g43,g5)
    c: Coincident(g43,g6)
    c: Coincident(g44,g7)
    c: Coincident(g44,g8)
    c: Coincident(g45,g7)
    c: Coincident(g45,g8)
    c: Distance(g30) = 256
    c: Distance(g33) = 100
FEATURE [Part::Extrusion] Extrude002
  Base = -> Sketch001
  Dir = (1,0,0)
  DirMode = 2
  FaceMakerClass = Part::FaceMakerBullseye
  LengthFwd = 8
  LengthRev = 0
  Solid = true
  Symmetric = false
FEATURE [Sketcher::SketchObject] Sketch002
  FullyConstrained = true
  sketch-geometry (20):
    g0: LineSegment StartX=-2.77179 StartY=-200.304 StartZ=0 EndX=5.22821 EndY=-200.304 EndZ=0
    g1: LineSegment StartX=5.22821 StartY=-200.304 StartZ=0 EndX=5.22821 EndY=-197.304 EndZ=0
    g2: LineSegment StartX=-2.77179 StartY=-200.304 StartZ=0 EndX=-2.77179 EndY=-197.304 EndZ=0
    g3: LineSegment StartX=5.22821 StartY=-197.304 StartZ=0 EndX=8.22821 EndY=-197.304 EndZ=0
    g4: LineSegment StartX=-2.77179 StartY=-197.304 StartZ=0 EndX=-5.77179 EndY=-197.304 EndZ=0
    g5: LineSegment StartX=19.2282 StartY=-203.304 StartZ=0 EndX=19.2282 EndY=-206.304 EndZ=0
    g6: LineSegment StartX=-16.7718 StartY=-203.304 StartZ=0 EndX=-16.7718 EndY=-206.304 EndZ=0
    g7: LineSegment StartX=-16.7718 StartY=-206.304 StartZ=0 EndX=19.2282 EndY=-206.304 EndZ=0
    g8: Circle CenterX=-16.7718 CenterY=-203.304 CenterZ=0 NormalX=0 NormalY=0 NormalZ=1 AngleXU=0 Radius=1
    g9: Circle CenterX=-5.77179 CenterY=-203.304 CenterZ=0 NormalX=0 NormalY=0 NormalZ=1 AngleXU=0 Radius=1
    g10: Circle CenterX=-5.77179 CenterY=-197.304 CenterZ=0 NormalX=0 NormalY=0 NormalZ=1 AngleXU=0 Radius=1
    g11: BSplineCurve PolesCount=3 KnotsCount=2 Degree=2 IsPeriodic=0
    g12: GeomPoint X=-16.7718 Y=-203.304 Z=0
    g13: GeomPoint X=-5.77179 Y=-197.304 Z=0
    g14: Circle CenterX=19.2282 CenterY=-203.304 CenterZ=0 NormalX=0 NormalY=0 NormalZ=1 AngleXU=0 Radius=1
    g15: Circle CenterX=8.22821 CenterY=-203.304 CenterZ=0 NormalX=0 NormalY=0 NormalZ=1 AngleXU=0 Radius=1
    g16: Circle CenterX=8.22821 CenterY=-197.304 CenterZ=0 NormalX=0 NormalY=0 NormalZ=1 AngleXU=0 Radius=1
    g17: BSplineCurve PolesCount=3 KnotsCount=2 Degree=2 IsPeriodic=0
    g18: GeomPoint X=19.2282 Y=-203.304 Z=0
    g19: GeomPoint X=8.22821 Y=-197.304 Z=0
  constraints (41):
    c: Horizontal(g0)
    c: Distance(g0) = 8
    c: Coincident(g1,g0)
    c: Vertical(g1)
    c: Distance(g1) = 3
    c: Coincident(g2,g0)
    c: Vertical(g2)
    c: Distance(g2) = 3
    c: Coincident(g3,g1)
    c: Horizontal(g3)
    c: Distance(g3) = 3
    c: Coincident(g4,g2)
    c: Horizontal(g4)
    c: Distance(g4) = 3
    c: Vertical(g5)
    c: Vertical(g6)
    c: Coincident(g7,g6)
    c: Coincident(g7,g5)
    c: Weight(g8) = 1
    c: Equal(g8,g9)
    c: Equal(g8,g10)
    c: Coincident(g11,g4)
    c: InternalAlignment(g8,g11)
    c: InternalAlignment(g9,g11)
    c: InternalAlignment(g10,g11)
    c: InternalAlignment(g12,g11)
    c: InternalAlignment(g13,g11)
    c: Coincident(g17,g5)
    c: Weight(g14) = 1
    c: Equal(g14,g15)
    c: Equal(g14,g16)
    c: Coincident(g17,g3)
    c: InternalAlignment(g14,g17)
    c: InternalAlignment(g15,g17)
    c: InternalAlignment(g16,g17)
    c: InternalAlignment(g18,g17)
    c: InternalAlignment(g19,g17)
    c: Block(g7)
    c: Block(g17)
    c: Block(g11)
    c: Block(g6)
FEATURE [Part::Extrusion] Extrude003
  Base = -> Sketch002
  Dir = (0,0,1)
  DirMode = 2
  FaceMakerClass = Part::FaceMakerBullseye
  LengthFwd = 260
  LengthRev = 0
  Solid = true
  Symmetric = false
FEATURE [Part::Extrusion] Extrude
  Base = -> Sketch
  Dir = (0,0,1)
  DirMode = 2
  FaceMakerClass = Part::FaceMakerBullseye
  LengthFwd = 14
  LengthRev = 0
  Solid = true
  Symmetric = false
